# Revit family: 0510212_DS
name_source: partatom
category: Air Terminals
revit_build: Autodesk Revit MEP 2012 (Build: 20110309_2315(x64)
units: mm (PartAtom-declared; Revit-internal decimal feet)

## types (8) — shared parameters
Cuello Mín-Máx Redondo = 6" a 20" en incrementos de 2"
Description = Difusor  de largo alcance
Dirección de descarga = Ajustable de 0° a 38°
Función = Inyección
Manufacturer = INNES
Material = Aluminio
Model = DS
Nota1 = .
Posición de Instalación = Muro
Tipo de Cuello = Redondo
Type Comments = Con compuerta de regulación
URL = https://www.innes.com.mx
Visible_Texto = No

## per-type parameters (varying)
| type | Conect | Medida_Requerida | Var_MR |
| DS-06" | 2.93 " | 6 " | 6 " |
| DS-08" | 4.12 " | 8 " | 8 " |
| DS-10" | 5.18 " | 10 " | 10 " |
| DS-12" | 6.02 " | 12 " | 12 " |
| DS-14" | 6.09 " | 14 " | 14 " |
| DS-16" | 8.07 " | 16 " | 16 " |
| DS-18" | 9.61 " | 18 " | 18 " |
| DS-20" | 9.61 " | 20 " | 20 " |

## geometry (parser evidence)
native form markers: Sweep x7
no freeform markers — native parametric forms only
